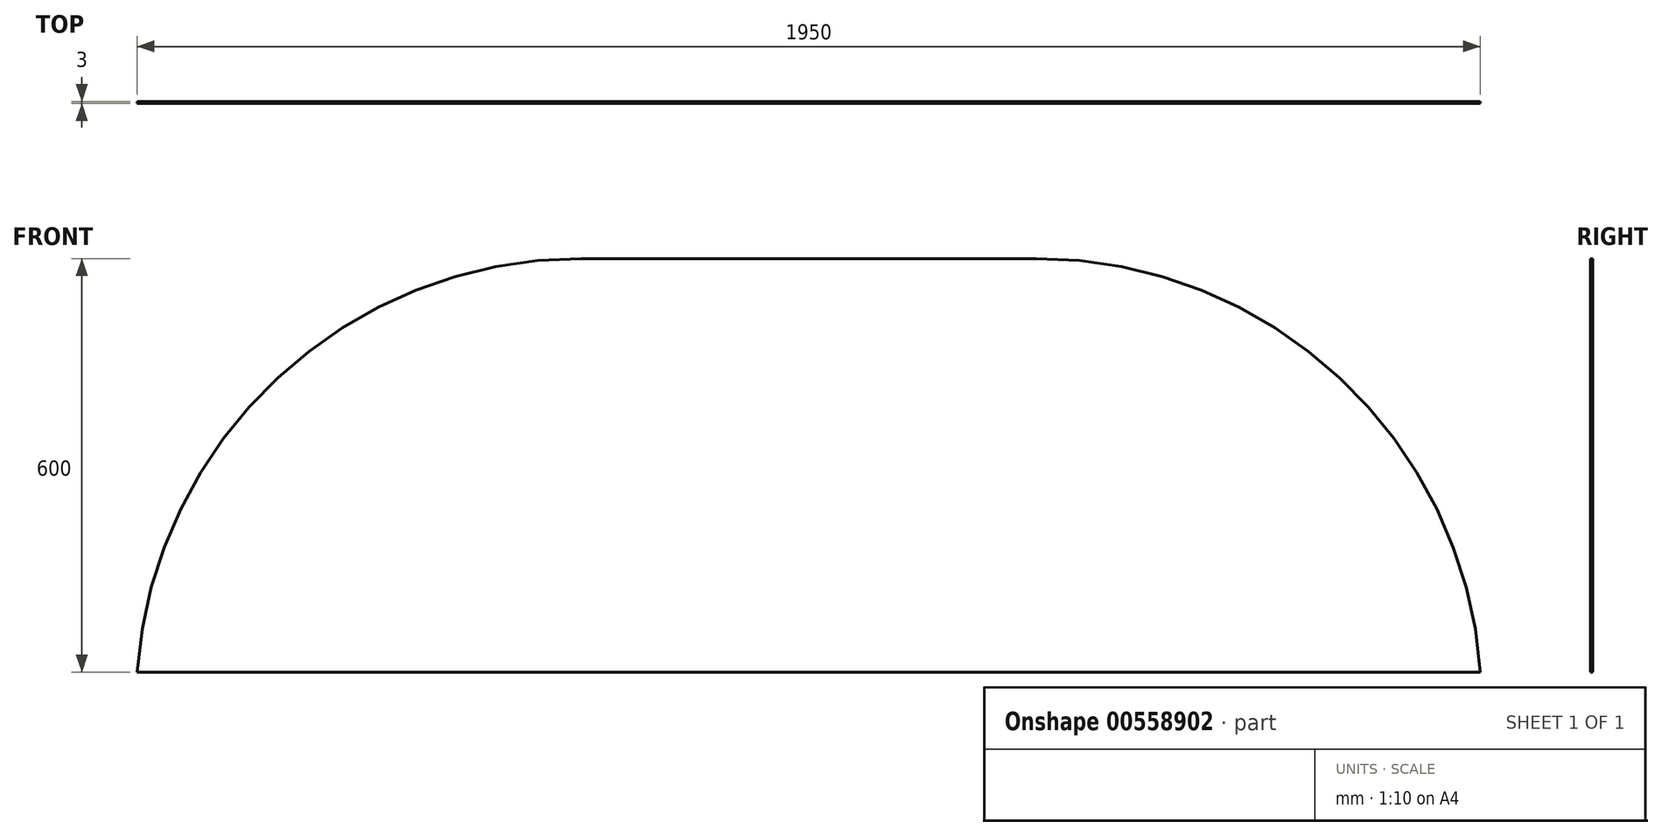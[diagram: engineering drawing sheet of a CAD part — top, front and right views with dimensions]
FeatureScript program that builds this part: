
annotation { "Feature Type Name" : "Feature", "Feature Type Description" : "" }
export const myFeature = defineFeature(function(context is Context, id is Id, definition is map)
    precondition{}
    {
        {
            var Q0;
            Q0=qCreatedBy(makeId("Front.planeOp"),FACE);
            var sketch = newSketch(context, id + "F0", { "sketchPlane" : qUnion([Q0])});
            skLineSegment(sketch, "E0.bottom", {"start": v(0, 0) * mm, "end": v(660, 0) * mm});
            skLineSegment(sketch, "E0.top", {"start": v(0, 600) * mm, "end": v(660, 600) * mm});
            skLineSegment(sketch, "E0.left", {"start": v(0, 0) * mm, "end": v(0, 600) * mm, "construction": true});
            skLineSegment(sketch, "E0.right", {"start": v(660, 0) * mm, "end": v(660, 600) * mm, "construction": true});
            skLineSegment(sketch, "E1", {"start": v(0, 0) * mm, "end": v(-645, 0) * mm});
            skArc(sketch, "E2", {"start": v(0, 600) * mm, "mid": v(-440.46, 426.8) * mm, "end": v(-645, 0) * mm});
            skLineSegment(sketch, "E3", {"start": v(660, 0) * mm, "end": v(1305, 0) * mm});
            skArc(sketch, "E4", {"start": v(1305, 0) * mm, "mid": v(1100.46, 426.8) * mm, "end": v(660, 600) * mm});
            skSolve(sketch);
        }
        {
            var Q0;
            Q0 = qSketchRegion(id + "F0", true);
            var Q1;
            Q1=makeQuery(id+"F0.imprint","IMPRINT",FACE,{"disambiguationData":[TD([[makeQuery(id+"F0.imprint","IMPRINT",EDGE,{"derivedFrom":sQuery(id+"F0.wireOp",EDGE,"E0.bottom")}),1.0]])]});
            extrude(context, id + "F1", {"entities" : qUnion([Q0, Q1]), "depth" : 3 * mm, "offsetDistance" : 25 * mm});
        }
    });
